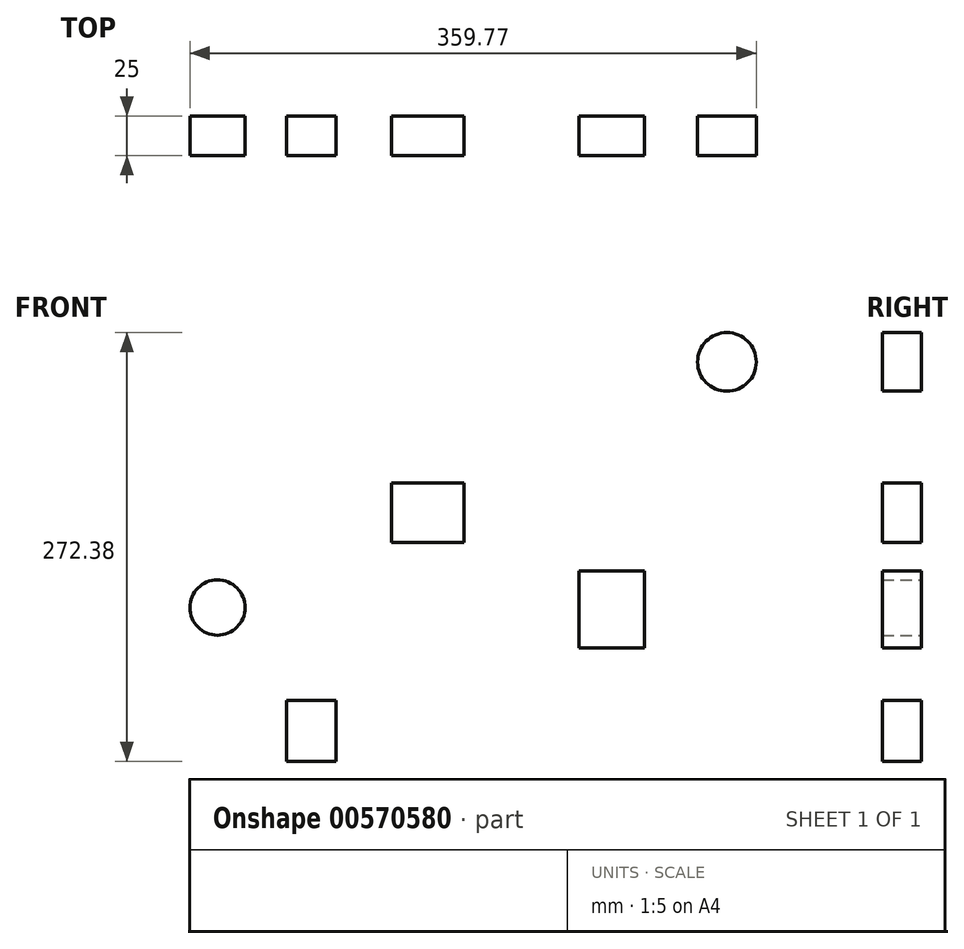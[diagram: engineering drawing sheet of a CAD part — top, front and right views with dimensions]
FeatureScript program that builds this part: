
annotation { "Feature Type Name" : "Feature", "Feature Type Description" : "" }
export const myFeature = defineFeature(function(context is Context, id is Id, definition is map)
    precondition{}
    {
        {
            var Q0;
            Q0=qCreatedBy(makeId("Front.planeOp"),FACE);
            var sketch = newSketch(context, id + "F0", { "sketchPlane" : qUnion([Q0])});
            skLineSegment(sketch, "E0.bottom", {"start": v(-87.96, 70.03) * mm, "end": v(-42.2, 70.03) * mm});
            skLineSegment(sketch, "E0.top", {"start": v(-87.96, 32.28) * mm, "end": v(-42.2, 32.28) * mm});
            skLineSegment(sketch, "E0.left", {"start": v(-87.96, 70.03) * mm, "end": v(-87.96, 32.28) * mm});
            skLineSegment(sketch, "E0.right", {"start": v(-42.2, 70.03) * mm, "end": v(-42.2, 32.28) * mm});
            skLineSegment(sketch, "E1.bottom", {"start": v(30.83, 14.42) * mm, "end": v(72.7, 14.42) * mm});
            skLineSegment(sketch, "E1.top", {"start": v(30.83, -34.51) * mm, "end": v(72.7, -34.51) * mm});
            skLineSegment(sketch, "E1.left", {"start": v(30.83, 14.42) * mm, "end": v(30.83, -34.51) * mm});
            skLineSegment(sketch, "E1.right", {"start": v(72.7, 14.42) * mm, "end": v(72.7, -34.51) * mm});
            skLineSegment(sketch, "E2.bottom", {"start": v(-154.81, -68.06) * mm, "end": v(-123.33, -68.06) * mm});
            skLineSegment(sketch, "E2.top", {"start": v(-154.81, -106.68) * mm, "end": v(-123.33, -106.68) * mm});
            skLineSegment(sketch, "E2.left", {"start": v(-154.81, -68.06) * mm, "end": v(-154.81, -106.68) * mm});
            skLineSegment(sketch, "E2.right", {"start": v(-123.33, -68.06) * mm, "end": v(-123.33, -106.68) * mm});
            skCircle(sketch, "E3", {"center": v(124.95, 147.07) * mm, "radius": 18.63 * mm});
            skCircle(sketch, "E4", {"center": v(-198.63, -8.98) * mm, "radius": 17.55 * mm});
            skSolve(sketch);
        }
        {
            var Q0;
            Q0 = qSketchRegion(id + "F0", true);
            extrude(context, id + "F1", {"entities" : qUnion([Q0]), "depth" : 25 * mm, "offsetDistance" : 25 * mm});
        }
    });
